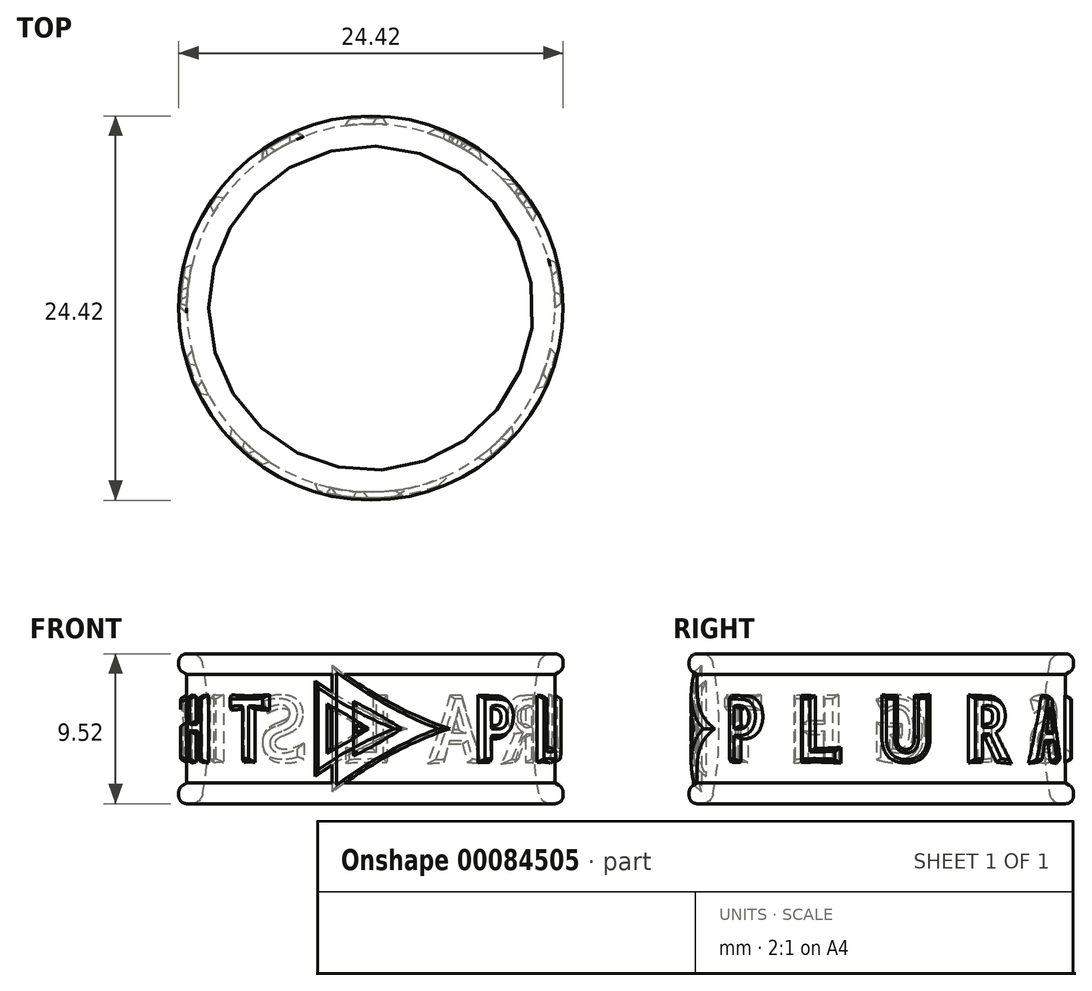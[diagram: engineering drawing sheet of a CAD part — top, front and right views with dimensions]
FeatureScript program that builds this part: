
annotation { "Feature Type Name" : "Feature", "Feature Type Description" : "" }
export const myFeature = defineFeature(function(context is Context, id is Id, definition is map)
    precondition{}
    {
        {
            var Q0;
            Q0=qCreatedBy(makeId("Front.planeOp"),FACE);
            var sketch = newSketch(context, id + "F0", { "sketchPlane" : qUnion([Q0])});
            skLineSegment(sketch, "E0", {"start": v(0, 0) * mm, "end": v(0, 5.68) * mm, "construction": true});
            skLineSegment(sketch, "E1", {"start": v(0, 0) * mm, "end": v(32.88, 0) * mm, "construction": true});
            skLineSegment(sketch, "E2", {"start": v(11.7, 0) * mm, "end": v(11.7, 3.45) * mm});
            skLineSegment(sketch, "E3", {"start": v(11.7, 3.45) * mm, "end": v(12.2, 3.75) * mm});
            skLineSegment(sketch, "E4", {"start": v(12.2, 3.75) * mm, "end": v(12.2, 4.76) * mm});
            skLineSegment(sketch, "E5", {"start": v(12.2, 4.76) * mm, "end": v(10.8, 4.76) * mm});
            skArc(sketch, "E6", {"start": v(10.8, 4.76) * mm, "mid": v(10.43, 2.4) * mm, "end": v(10.3, 0) * mm});
            skLineSegment(sketch, "E7.MirrorCS", {"start": v(11.7, -3.45) * mm, "end": v(12.2, -3.75) * mm});
            skLineSegment(sketch, "E8.MirrorCS", {"start": v(11.7, 0) * mm, "end": v(11.7, -3.45) * mm});
            skLineSegment(sketch, "E9.MirrorCS", {"start": v(12.2, -3.75) * mm, "end": v(12.2, -4.76) * mm});
            skArc(sketch, "E10.MirrorCS", {"start": v(10.8, -4.76) * mm, "mid": v(10.43, -2.4) * mm, "end": v(10.3, 0) * mm});
            skLineSegment(sketch, "E11.MirrorCS", {"start": v(12.2, -4.76) * mm, "end": v(10.8, -4.76) * mm});
            skSolve(sketch);
        }
        {
            var Q0;
            Q0=makeQuery(id+"F0.imprint","IMPRINT",FACE,{"disambiguationData":[TD([[makeQuery(id+"F0.imprint","IMPRINT",EDGE,{"derivedFrom":sQuery(id+"F0.wireOp",EDGE,"E2")}),1.0]])]});
            var Q1;
            Q1=sQuery(id+"F0.wireOp",EDGE,"E0");
            revolve(context, id + "F1", {"entities" : qUnion([Q0]), "axis" : qUnion([Q1]), "revolveType" : RevolveType.FULL});
        }
        {
            var Q0;
            Q0=qCreatedBy(makeId("Top.planeOp"),FACE);
            var sketch = newSketch(context, id + "F2", { "sketchPlane" : qUnion([Q0])});
            skCircle(sketch, "E12.cCircle", {"center": v(0, 0) * mm, "radius": 12.08 * mm, "construction": true});
            skLineSegment(sketch, "E12.0", {"start": v(9.94, 6.86) * mm, "end": v(11.99, 1.46) * mm});
            skLineSegment(sketch, "E12.1", {"start": v(11.99, 1.46) * mm, "end": v(11.3, -4.28) * mm});
            skLineSegment(sketch, "E12.2", {"start": v(11.3, -4.28) * mm, "end": v(8, -9.04) * mm});
            skLineSegment(sketch, "E12.3", {"start": v(8, -9.04) * mm, "end": v(2.9, -11.73) * mm});
            skLineSegment(sketch, "E12.4", {"start": v(2.9, -11.73) * mm, "end": v(-2.9, -11.73) * mm});
            skLineSegment(sketch, "E12.5", {"start": v(-2.9, -11.73) * mm, "end": v(-8, -9.04) * mm});
            skLineSegment(sketch, "E12.6", {"start": v(-8, -9.04) * mm, "end": v(-11.3, -4.28) * mm});
            skLineSegment(sketch, "E12.7", {"start": v(-11.3, -4.28) * mm, "end": v(-11.99, 1.46) * mm});
            skLineSegment(sketch, "E12.8", {"start": v(-11.99, 1.46) * mm, "end": v(-9.94, 6.86) * mm});
            skLineSegment(sketch, "E12.9", {"start": v(-9.94, 6.86) * mm, "end": v(-5.61, 10.7) * mm});
            skLineSegment(sketch, "E12.10", {"start": v(-5.61, 10.7) * mm, "end": v(0, 12.08) * mm});
            skLineSegment(sketch, "E12.11", {"start": v(0, 12.08) * mm, "end": v(5.61, 10.7) * mm});
            skLineSegment(sketch, "E12.12", {"start": v(5.61, 10.7) * mm, "end": v(9.94, 6.86) * mm});
            skCircle(sketch, "E13", {"center": v(0, 0) * mm, "radius": 12.33 * mm, "construction": true});
            skLineSegment(sketch, "E14", {"start": v(0, 0) * mm, "end": v(0.65, -12.32) * mm});
            skLineSegment(sketch, "E15", {"start": v(0, 0) * mm, "end": v(0, -12.33) * mm});
            skLineSegment(sketch, "E16", {"start": v(0, 0) * mm, "end": v(-1.68, -11.96) * mm});
            skLineSegment(sketch, "E17", {"start": v(0, 0) * mm, "end": v(8, -9.04) * mm});
            skLineSegment(sketch, "E18", {"start": v(0, 0) * mm, "end": v(11.3, -4.28) * mm});
            skLineSegment(sketch, "E19", {"start": v(0, 0) * mm, "end": v(11.99, 1.46) * mm});
            skLineSegment(sketch, "E20", {"start": v(0, 0) * mm, "end": v(9.94, 6.86) * mm});
            skLineSegment(sketch, "E21", {"start": v(0, 0) * mm, "end": v(5.61, 10.7) * mm});
            skLineSegment(sketch, "E22", {"start": v(0, 0) * mm, "end": v(0, 12.08) * mm});
            skLineSegment(sketch, "E23", {"start": v(0, 0) * mm, "end": v(-9.94, 6.86) * mm});
            skLineSegment(sketch, "E24", {"start": v(0, 0) * mm, "end": v(-11.3, -4.28) * mm});
            skLineSegment(sketch, "E25", {"start": v(0, 0) * mm, "end": v(-5.61, 10.7) * mm});
            skLineSegment(sketch, "E26", {"start": v(0, 0) * mm, "end": v(-11.99, 1.46) * mm});
            skLineSegment(sketch, "E27", {"start": v(0, 0) * mm, "end": v(-8, -9.04) * mm});
            skSolve(sketch);
        }
        {
            var Q0;
            Q0=sQuery(id+"F2.wireOp",VERTEX,"E15.end");
            var Q1;
            Q1=sQuery(id+"F2.wireOp",EDGE,"E15");
            cPlane(context, id + "F3", {"entities" : qUnion([Q0, Q1]), "cplaneType" : CPlaneType.LINE_POINT, "offset" : 152.4 * mm, "width" : 152.4 * mm, "height" : 152.4 * mm});
        }
        {
            var Q0;
            Q0=sQuery(id+"F2.wireOp",EDGE,"E16");
            var Q1;
            Q1=sQuery(id+"F2.wireOp",VERTEX,"E16.end");
            cPlane(context, id + "F4", {"entities" : qUnion([Q0, Q1]), "cplaneType" : CPlaneType.LINE_POINT, "offset" : 152.4 * mm, "width" : 152.4 * mm, "height" : 152.4 * mm});
        }
        {
            var Q0;
            Q0=qCreatedBy(id+"F4.planeOp",FACE);
            var sketch = newSketch(context, id + "F5", { "sketchPlane" : qUnion([Q0])});
            skLineSegment(sketch, "E28", {"start": v(2.67, 0) * mm, "end": v(-1.65, 2.5) * mm});
            skLineSegment(sketch, "E29", {"start": v(-1.65, 2.5) * mm, "end": v(-1.65, 0) * mm});
            skLineSegment(sketch, "E30.0", {"start": v(-1.14, 1.61) * mm, "end": v(-1.14, 0) * mm});
            skLineSegment(sketch, "E30.1", {"start": v(1.65, 0) * mm, "end": v(-1.14, 1.61) * mm});
            skLineSegment(sketch, "E31.MirrorCS", {"start": v(-1.14, -1.61) * mm, "end": v(-1.14, 0) * mm});
            skLineSegment(sketch, "E32.MirrorCS", {"start": v(-1.65, -2.5) * mm, "end": v(-1.65, 0) * mm});
            skLineSegment(sketch, "E33.MirrorCS", {"start": v(1.65, 0) * mm, "end": v(-1.14, -1.61) * mm});
            skLineSegment(sketch, "E34.MirrorCS", {"start": v(2.67, 0) * mm, "end": v(-1.65, -2.5) * mm});
            skSolve(sketch);
        }
        {
            var Q0;
            Q0 = qSketchRegion(id + "F5", true);
            extrude(context, id + "F6", {"entities" : qUnion([Q0]), "operationType" : NewBodyOperationType.ADD, "endBound" : BoundingType.UP_TO_NEXT, "oppositeDirection" : true, "depth" : 25.4 * mm, "hasDraft" : true, "draftAngle" : 30 * degree});
        }
        {
            var Q0;
            Q0=sQuery(id+"F2.wireOp",EDGE,"E14");
            var Q1;
            Q1=sQuery(id+"F2.wireOp",VERTEX,"E14.end");
            cPlane(context, id + "F7", {"entities" : qUnion([Q0, Q1]), "cplaneType" : CPlaneType.LINE_POINT, "offset" : 152.4 * mm, "width" : 152.4 * mm, "height" : 152.4 * mm});
        }
        {
            var Q0;
            Q0=qCreatedBy(id+"F7.planeOp",FACE);
            var sketch = newSketch(context, id + "F8", { "sketchPlane" : qUnion([Q0])});
            skLineSegment(sketch, "E35", {"start": v(2.72, 0) * mm, "end": v(-2.45, 2.98) * mm});
            skLineSegment(sketch, "E36", {"start": v(-2.45, 2.98) * mm, "end": v(-2.45, 0) * mm});
            skLineSegment(sketch, "E37.0", {"start": v(-1.94, 2.1) * mm, "end": v(-1.94, 0) * mm});
            skLineSegment(sketch, "E37.1", {"start": v(1.7, 0) * mm, "end": v(-1.94, 2.1) * mm});
            skLineSegment(sketch, "E38.MirrorCS", {"start": v(-1.94, -2.1) * mm, "end": v(-1.94, 0) * mm});
            skLineSegment(sketch, "E39.MirrorCS", {"start": v(1.7, 0) * mm, "end": v(-1.94, -2.1) * mm});
            skLineSegment(sketch, "E40.MirrorCS", {"start": v(-2.45, -2.98) * mm, "end": v(-2.45, 0) * mm});
            skLineSegment(sketch, "E41.MirrorCS", {"start": v(2.72, 0) * mm, "end": v(-2.45, -2.98) * mm});
            skSolve(sketch);
        }
        {
            var Q0;
            Q0 = qSketchRegion(id + "F8", true);
            var Q1;
            Q1=makeQuery(id+"F6.boolean.opBoolean","SPLIT",FACE,{"disambiguationData":[TD([makeQuery(id+"F1.opRevolve","SWEPT_FACE",FACE,{"disambiguationData":[OSD([sQuery(id+"F0.wireOp",EDGE,"E3")])]})])],"derivedFrom":makeQuery(id+"F1.opRevolve","SWEPT_FACE",FACE,{"disambiguationData":[OSD([sQuery(id+"F0.wireOp",EDGE,"E2"),sQuery(id+"F0.wireOp",EDGE,"E8.MirrorCS")])]})});
            extrude(context, id + "F9", {"entities" : qUnion([Q0]), "endBound" : BoundingType.UP_TO_SURFACE, "oppositeDirection" : true, "endBoundEntityFace" : qUnion([Q1]), "depth" : 25.4 * mm, "hasDraft" : true, "draftAngle" : 30 * degree});
        }
        {
            var Q0;
            Q0=sQuery(id+"F2.wireOp",EDGE,"E17");
            var Q1;
            Q1=sQuery(id+"F2.wireOp",VERTEX,"E12.3.start");
            cPlane(context, id + "F10", {"entities" : qUnion([Q0, Q1]), "cplaneType" : CPlaneType.LINE_POINT, "offset" : 152.4 * mm, "width" : 152.4 * mm, "height" : 152.4 * mm});
        }
        {
            var Q0;
            Q0=qCreatedBy(id+"F10.planeOp",FACE);
            var sketch = newSketch(context, id + "F11", { "sketchPlane" : qUnion([Q0])});
            skText(sketch, "E42", { "text": "P", "fontName": "DroidSansMono.ttf"});
            const initialGuessF11  = {"E42": [-0.00141, -0.0019, 1, 0, 0.00381]};
            skSetInitialGuess(sketch, initialGuessF11);
            skSolve(sketch);
        }
        {
            var Q0;
            Q0 = qSketchRegion(id + "F11", true);
            extrude(context, id + "F12", {"entities" : qUnion([Q0]), "operationType" : NewBodyOperationType.ADD, "endBound" : BoundingType.UP_TO_NEXT, "oppositeDirection" : true, "depth" : 25.4 * mm, "hasDraft" : true, "draftAngle" : 30 * degree});
        }
        {
            var Q0;
            Q0=sQuery(id+"F2.wireOp",VERTEX,"E12.2.start");
            var Q1;
            Q1=sQuery(id+"F2.wireOp",EDGE,"E18");
            cPlane(context, id + "F13", {"entities" : qUnion([Q0, Q1]), "cplaneType" : CPlaneType.LINE_POINT, "offset" : 152.4 * mm, "width" : 152.4 * mm, "height" : 152.4 * mm});
        }
        {
            var Q0;
            Q0=qCreatedBy(id+"F13.planeOp",FACE);
            var sketch = newSketch(context, id + "F14", { "sketchPlane" : qUnion([Q0])});
            skText(sketch, "E43", { "text": "L", "fontName": "DroidSansMono.ttf"});
            const initialGuessF14  = {"E43": [-0.00136, -0.0019, 1, 0, 0.00381]};
            skSetInitialGuess(sketch, initialGuessF14);
            skSolve(sketch);
        }
        {
            var Q0;
            Q0 = qSketchRegion(id + "F14", true);
            extrude(context, id + "F15", {"entities" : qUnion([Q0]), "operationType" : NewBodyOperationType.ADD, "endBound" : BoundingType.UP_TO_NEXT, "oppositeDirection" : true, "depth" : 25.4 * mm, "hasDraft" : true, "draftAngle" : 30 * degree});
        }
        {
            var Q0;
            Q0=sQuery(id+"F2.wireOp",VERTEX,"E12.1.start");
            var Q1;
            Q1=sQuery(id+"F2.wireOp",EDGE,"E19");
            cPlane(context, id + "F16", {"entities" : qUnion([Q0, Q1]), "cplaneType" : CPlaneType.LINE_POINT, "offset" : 152.4 * mm, "width" : 152.4 * mm, "height" : 152.4 * mm});
        }
        {
            var Q0;
            Q0=qCreatedBy(id+"F16.planeOp",FACE);
            var sketch = newSketch(context, id + "F17", { "sketchPlane" : qUnion([Q0])});
            skText(sketch, "E44", { "text": "U", "fontName": "DroidSansMono.ttf"});
            const initialGuessF17  = {"E44": [-0.00143, -0.0019, 1, 0, 0.00381]};
            skSetInitialGuess(sketch, initialGuessF17);
            skSolve(sketch);
        }
        {
            var Q0;
            Q0 = qSketchRegion(id + "F17", true);
            extrude(context, id + "F18", {"entities" : qUnion([Q0]), "operationType" : NewBodyOperationType.ADD, "endBound" : BoundingType.UP_TO_NEXT, "oppositeDirection" : true, "depth" : 25.4 * mm, "hasDraft" : true, "draftAngle" : 30 * degree});
        }
        {
            var Q0;
            Q0=sQuery(id+"F2.wireOp",VERTEX,"E12.12.end");
            var Q1;
            Q1=sQuery(id+"F2.wireOp",EDGE,"E20");
            cPlane(context, id + "F19", {"entities" : qUnion([Q0, Q1]), "cplaneType" : CPlaneType.LINE_POINT, "offset" : 152.4 * mm, "width" : 152.4 * mm, "height" : 152.4 * mm});
        }
        {
            var Q0;
            Q0=qCreatedBy(id+"F19.planeOp",FACE);
            var sketch = newSketch(context, id + "F20", { "sketchPlane" : qUnion([Q0])});
            skText(sketch, "E45", { "text": "R", "fontName": "DroidSansMono.ttf"});
            const initialGuessF20  = {"E45": [-0.00151, -0.0019, 1, 0, 0.00381]};
            skSetInitialGuess(sketch, initialGuessF20);
            skSolve(sketch);
        }
        {
            var Q0;
            Q0 = qSketchRegion(id + "F20", true);
            extrude(context, id + "F21", {"entities" : qUnion([Q0]), "operationType" : NewBodyOperationType.ADD, "endBound" : BoundingType.UP_TO_NEXT, "oppositeDirection" : true, "depth" : 25.4 * mm, "hasDraft" : true, "draftAngle" : 30 * degree});
        }
        {
            var Q0;
            Q0=sQuery(id+"F2.wireOp",EDGE,"E21");
            var Q1;
            Q1=sQuery(id+"F2.wireOp",VERTEX,"E21.end");
            cPlane(context, id + "F22", {"entities" : qUnion([Q0, Q1]), "cplaneType" : CPlaneType.LINE_POINT, "offset" : 152.4 * mm, "width" : 152.4 * mm, "height" : 152.4 * mm});
        }
        {
            var Q0;
            Q0=qCreatedBy(id+"F22.planeOp",FACE);
            var sketch = newSketch(context, id + "F23", { "sketchPlane" : qUnion([Q0])});
            skText(sketch, "E46", { "text": "A", "fontName": "DroidSansMono.ttf"});
            const initialGuessF23  = {"E46": [-0.00155, -0.0019, 1, 0, 0.00381]};
            skSetInitialGuess(sketch, initialGuessF23);
            skSolve(sketch);
        }
        {
            var Q0;
            Q0 = qSketchRegion(id + "F23", true);
            extrude(context, id + "F24", {"entities" : qUnion([Q0]), "operationType" : NewBodyOperationType.ADD, "endBound" : BoundingType.UP_TO_NEXT, "oppositeDirection" : true, "depth" : 25.4 * mm, "hasDraft" : true, "draftAngle" : 30 * degree});
        }
        {
            var Q0;
            Q0=sQuery(id+"F2.wireOp",EDGE,"E22");
            var Q1;
            Q1=sQuery(id+"F2.wireOp",VERTEX,"E12.11.start");
            cPlane(context, id + "F25", {"entities" : qUnion([Q0, Q1]), "cplaneType" : CPlaneType.LINE_POINT, "offset" : 152.4 * mm, "width" : 152.4 * mm, "height" : 152.4 * mm});
        }
        {
            var Q0;
            Q0=qCreatedBy(id+"F25.planeOp",FACE);
            var sketch = newSketch(context, id + "F26", { "sketchPlane" : qUnion([Q0])});
            skText(sketch, "E47", { "text": "L", "fontName": "OpenSans-Regular.ttf"});
            const initialGuessF26  = {"E47": [-0.00131, -0.0019, 1, 0, 0.00381]};
            skSetInitialGuess(sketch, initialGuessF26);
            skSolve(sketch);
        }
        {
            var Q0;
            Q0 = qSketchRegion(id + "F26", true);
            extrude(context, id + "F27", {"entities" : qUnion([Q0]), "operationType" : NewBodyOperationType.ADD, "endBound" : BoundingType.UP_TO_NEXT, "oppositeDirection" : true, "depth" : 25.4 * mm, "hasDraft" : true, "draftAngle" : 30 * degree});
        }
        {
            var Q0;
            Q0=sQuery(id+"F2.wireOp",VERTEX,"E12.10.start");
            var Q1;
            Q1=sQuery(id+"F2.wireOp",EDGE,"E25");
            cPlane(context, id + "F28", {"entities" : qUnion([Q0, Q1]), "cplaneType" : CPlaneType.LINE_POINT, "offset" : 152.4 * mm, "width" : 152.4 * mm, "height" : 152.4 * mm});
        }
        {
            var Q0;
            Q0=qCreatedBy(id+"F28.planeOp",FACE);
            var sketch = newSketch(context, id + "F29", { "sketchPlane" : qUnion([Q0])});
            skText(sketch, "E48", { "text": "S", "fontName": "DroidSansMono.ttf"});
            const initialGuessF29  = {"E48": [-0.0014, -0.0019, 1, 0, 0.00381]};
            skSetInitialGuess(sketch, initialGuessF29);
            skSolve(sketch);
        }
        {
            var Q0;
            Q0 = qSketchRegion(id + "F29", true);
            extrude(context, id + "F30", {"entities" : qUnion([Q0]), "operationType" : NewBodyOperationType.ADD, "endBound" : BoundingType.UP_TO_NEXT, "oppositeDirection" : true, "depth" : 25.4 * mm, "hasDraft" : true, "draftAngle" : 30 * degree});
        }
        {
            var Q0;
            Q0=sQuery(id+"F2.wireOp",EDGE,"E23");
            var Q1;
            Q1=sQuery(id+"F2.wireOp",VERTEX,"E12.9.start");
            cPlane(context, id + "F31", {"entities" : qUnion([Q0, Q1]), "cplaneType" : CPlaneType.LINE_POINT, "offset" : 152.4 * mm, "width" : 152.4 * mm, "height" : 152.4 * mm});
        }
        {
            var Q0;
            Q0=qCreatedBy(id+"F31.planeOp",FACE);
            var sketch = newSketch(context, id + "F32", { "sketchPlane" : qUnion([Q0])});
            skText(sketch, "E49", { "text": "I", "fontName": "AllertaStencil-Regular.ttf"});
            skLineSegment(sketch, "E50", {"start": v(0.42, 0) * mm, "end": v(-0.42, 0) * mm, "construction": true});
            const initialGuessF32  = {"E49": [-0.0007, -0.0019, 1, 0, 0.00381]};
            skSetInitialGuess(sketch, initialGuessF32);
            skSolve(sketch);
        }
        {
            var Q0;
            Q0 = qSketchRegion(id + "F32", true);
            extrude(context, id + "F33", {"entities" : qUnion([Q0]), "operationType" : NewBodyOperationType.ADD, "endBound" : BoundingType.UP_TO_NEXT, "oppositeDirection" : true, "depth" : 25.4 * mm, "hasDraft" : true, "draftAngle" : 30 * degree});
        }
        {
            var Q0;
            Q0=sQuery(id+"F2.wireOp",EDGE,"E26");
            var Q1;
            Q1=sQuery(id+"F2.wireOp",VERTEX,"E12.8.start");
            cPlane(context, id + "F34", {"entities" : qUnion([Q0, Q1]), "cplaneType" : CPlaneType.LINE_POINT, "offset" : 152.4 * mm, "width" : 152.4 * mm, "height" : 152.4 * mm});
        }
        {
            var Q0;
            Q0=qCreatedBy(id+"F34.planeOp",FACE);
            var sketch = newSketch(context, id + "F35", { "sketchPlane" : qUnion([Q0])});
            skText(sketch, "E51", { "text": "G", "fontName": "DroidSansMono.ttf"});
            const initialGuessF35  = {"E51": [-0.00141, -0.0019, 1, 0, 0.00381]};
            skSetInitialGuess(sketch, initialGuessF35);
            skSolve(sketch);
        }
        {
            var Q0;
            Q0 = qSketchRegion(id + "F35", true);
            extrude(context, id + "F36", {"entities" : qUnion([Q0]), "operationType" : NewBodyOperationType.ADD, "endBound" : BoundingType.UP_TO_NEXT, "oppositeDirection" : true, "depth" : 25.4 * mm, "hasDraft" : true, "draftAngle" : 30 * degree});
        }
        {
            var Q0;
            Q0=sQuery(id+"F2.wireOp",EDGE,"E24");
            var Q1;
            Q1=sQuery(id+"F2.wireOp",VERTEX,"E12.7.start");
            cPlane(context, id + "F37", {"entities" : qUnion([Q0, Q1]), "cplaneType" : CPlaneType.LINE_POINT, "offset" : 152.4 * mm, "width" : 152.4 * mm, "height" : 152.4 * mm});
        }
        {
            var Q0;
            Q0=qCreatedBy(id+"F37.planeOp",FACE);
            var sketch = newSketch(context, id + "F38", { "sketchPlane" : qUnion([Q0])});
            skText(sketch, "E52", { "text": "H", "fontName": "DroidSansMono.ttf"});
            skLineSegment(sketch, "E53", {"start": v(0, 0) * mm, "end": v(-0.15, 0) * mm, "construction": true});
            const initialGuessF38  = {"E52": [-0.00157, -0.0019, 1, 0, 0.0038]};
            skSetInitialGuess(sketch, initialGuessF38);
            skSolve(sketch);
        }
        {
            var Q0;
            Q0 = qSketchRegion(id + "F38", true);
            extrude(context, id + "F39", {"entities" : qUnion([Q0]), "operationType" : NewBodyOperationType.ADD, "endBound" : BoundingType.UP_TO_NEXT, "oppositeDirection" : true, "depth" : 25.4 * mm, "hasDraft" : true, "draftAngle" : 30 * degree});
        }
        {
            var Q0;
            Q0=sQuery(id+"F2.wireOp",EDGE,"E27");
            var Q1;
            Q1=sQuery(id+"F2.wireOp",VERTEX,"E27.end");
            cPlane(context, id + "F40", {"entities" : qUnion([Q0, Q1]), "cplaneType" : CPlaneType.LINE_POINT, "offset" : 152.4 * mm, "width" : 152.4 * mm, "height" : 152.4 * mm});
        }
        {
            var Q0;
            Q0=qCreatedBy(id+"F40.planeOp",FACE);
            var sketch = newSketch(context, id + "F41", { "sketchPlane" : qUnion([Q0])});
            skText(sketch, "E54", { "text": "T", "fontName": "DroidSansMono.ttf"});
            skLineSegment(sketch, "E55", {"start": v(0, 0) * mm, "end": v(-0.08, 0) * mm});
            const initialGuessF41  = {"E54": [-0.00153, -0.0019, 1, 0, 0.00381]};
            skSetInitialGuess(sketch, initialGuessF41);
            skSolve(sketch);
        }
        {
            var Q0;
            Q0 = qSketchRegion(id + "F41", true);
            extrude(context, id + "F42", {"entities" : qUnion([Q0]), "operationType" : NewBodyOperationType.ADD, "endBound" : BoundingType.UP_TO_NEXT, "oppositeDirection" : true, "depth" : 25.4 * mm, "hasDraft" : true, "draftAngle" : 30 * degree});
        }
        {
            var Q0;
            Q0=qCreatedBy(makeId("Top.planeOp"),FACE);
            var sketch = newSketch(context, id + "F43", { "sketchPlane" : qUnion([Q0])});
            skCircle(sketch, "E56.0", {"center": v(0, 0) * mm, "radius": 12.33 * mm});
            skCircle(sketch, "E57", {"center": v(0, 0) * mm, "radius": 18.18 * mm});
            skSolve(sketch);
        }
        {
            var Q0;
            Q0=qCreatedBy(makeId("Top.planeOp"),FACE);
            var sketch = newSketch(context, id + "F44", { "sketchPlane" : qUnion([Q0])});
            skCircle(sketch, "E58.0", {"center": v(0, 0) * mm, "radius": 12.08 * mm});
            skCircle(sketch, "E59.0", {"center": v(0, 0) * mm, "radius": 18.43 * mm});
            skSolve(sketch);
        }
        {
            var Q0;
            Q0=makeQuery(id+"F44.imprint","IMPRINT",FACE,{"disambiguationData":[TD([[makeQuery(id+"F44.imprint","IMPRINT",EDGE,{"derivedFrom":sQuery(id+"F44.wireOp",EDGE,"E58.0")}),-1.0]])]});
            extrude(context, id + "F45", {"entities" : qUnion([Q0]), "operationType" : NewBodyOperationType.REMOVE, "oppositeDirection" : true, "depth" : 3.56 * mm, "hasSecondDirection" : true, "secondDirectionOppositeDirection" : false, "secondDirectionDepth" : 3.56 * mm});
        }
        {
            var Q0;
            Q0=makeQuery(id+"F43.imprint","IMPRINT",FACE,{"disambiguationData":[TD([[makeQuery(id+"F43.imprint","IMPRINT",EDGE,{"derivedFrom":sQuery(id+"F43.wireOp",EDGE,"E56.0")}),-1.0]])]});
            extrude(context, id + "F46", {"entities" : qUnion([Q0]), "operationType" : NewBodyOperationType.REMOVE, "endBound" : BoundingType.THROUGH_ALL, "oppositeDirection" : true, "depth" : 25.4 * mm, "hasSecondDirection" : true, "secondDirectionBound" : BoundingType.THROUGH_ALL, "secondDirectionOppositeDirection" : false, "secondDirectionDepth" : 25.4 * mm});
        }
        {
            var Q0;
            Q0=makeQuery(id+"F1.opRevolve","SWEPT_EDGE",EDGE,{"disambiguationData":[OSD([sQuery(id+"F0.wireOp",EDGE,"E5"),sQuery(id+"F0.wireOp",EDGE,"E6")])]});
            var Q1;
            Q1=makeQuery(id+"F1.opRevolve","SWEPT_EDGE",EDGE,{"disambiguationData":[OSD([sQuery(id+"F0.wireOp",EDGE,"E10.MirrorCS"),sQuery(id+"F0.wireOp",EDGE,"E11.MirrorCS")])]});
            fillet(context, id + "F47", {"entities" : qUnion([Q0, Q1]), "radius" : 0.76 * mm, "tangentPropagation" : true, "allowEdgeOverflow" : false});
        }
        {
            var Q0;
            Q0=makeQuery(id+"F1.opRevolve","SWEPT_EDGE",EDGE,{"disambiguationData":[OSD([sQuery(id+"F0.wireOp",EDGE,"E4"),sQuery(id+"F0.wireOp",EDGE,"E5")])]});
            var Q1;
            Q1=makeQuery(id+"F1.opRevolve","SWEPT_EDGE",EDGE,{"disambiguationData":[OSD([sQuery(id+"F0.wireOp",EDGE,"E3"),sQuery(id+"F0.wireOp",EDGE,"E4")])]});
            var Q2;
            Q2=makeQuery(id+"F1.opRevolve","SWEPT_EDGE",EDGE,{"disambiguationData":[OSD([sQuery(id+"F0.wireOp",EDGE,"E7.MirrorCS"),sQuery(id+"F0.wireOp",EDGE,"E9.MirrorCS")])]});
            var Q3;
            Q3=makeQuery(id+"F1.opRevolve","SWEPT_EDGE",EDGE,{"disambiguationData":[OSD([sQuery(id+"F0.wireOp",EDGE,"E9.MirrorCS"),sQuery(id+"F0.wireOp",EDGE,"E11.MirrorCS")])]});
            fillet(context, id + "F48", {"entities" : qUnion([Q0, Q1, Q2, Q3]), "radius" : 0.5 * mm, "tangentPropagation" : true, "allowEdgeOverflow" : false});
        }
    });
